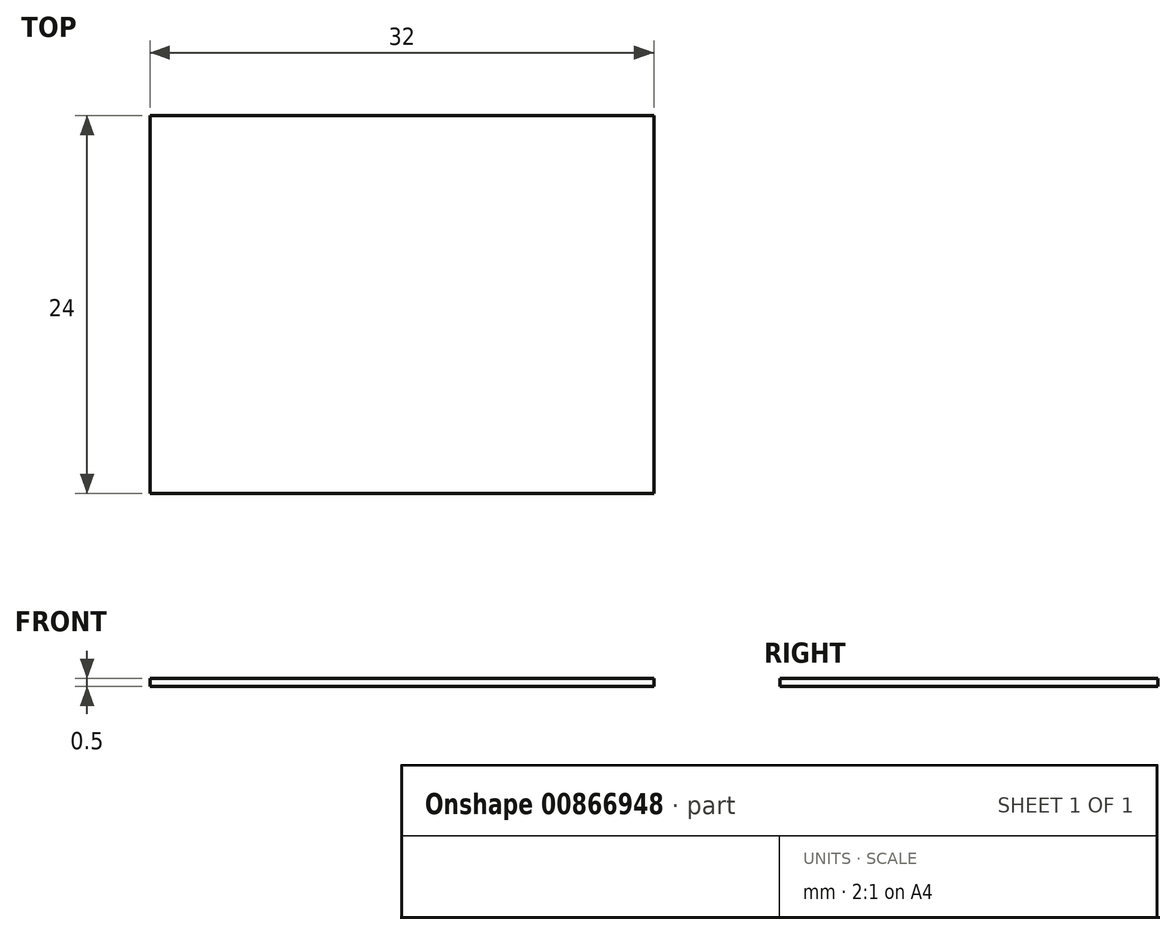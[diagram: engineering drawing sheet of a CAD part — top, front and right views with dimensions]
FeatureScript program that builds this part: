
annotation { "Feature Type Name" : "Feature", "Feature Type Description" : "" }
export const myFeature = defineFeature(function(context is Context, id is Id, definition is map)
    precondition{}
    {
        {
            var Q0;
            Q0=qCreatedBy(makeId("Top.planeOp"),FACE);
            var sketch = newSketch(context, id + "F0", { "sketchPlane" : qUnion([Q0])});
            skLineSegment(sketch, "E0.bottom", {"start": v(-16, -12) * mm, "end": v(16, -12) * mm});
            skLineSegment(sketch, "E0.top", {"start": v(-16, 12) * mm, "end": v(16, 12) * mm});
            skLineSegment(sketch, "E0.left", {"start": v(-16, -12) * mm, "end": v(-16, 12) * mm});
            skLineSegment(sketch, "E0.right", {"start": v(16, -12) * mm, "end": v(16, 12) * mm});
            skLineSegment(sketch, "E1", {"start": v(-16, 12) * mm, "end": v(16, -12) * mm, "construction": true});
            skSolve(sketch);
        }
        {
            var Q0;
            Q0 = qSketchRegion(id + "F0", true);
            extrude(context, id + "F1", {"entities" : qUnion([Q0]), "depth" : 0.5 * mm, "offsetDistance" : 25 * mm});
        }
    });
